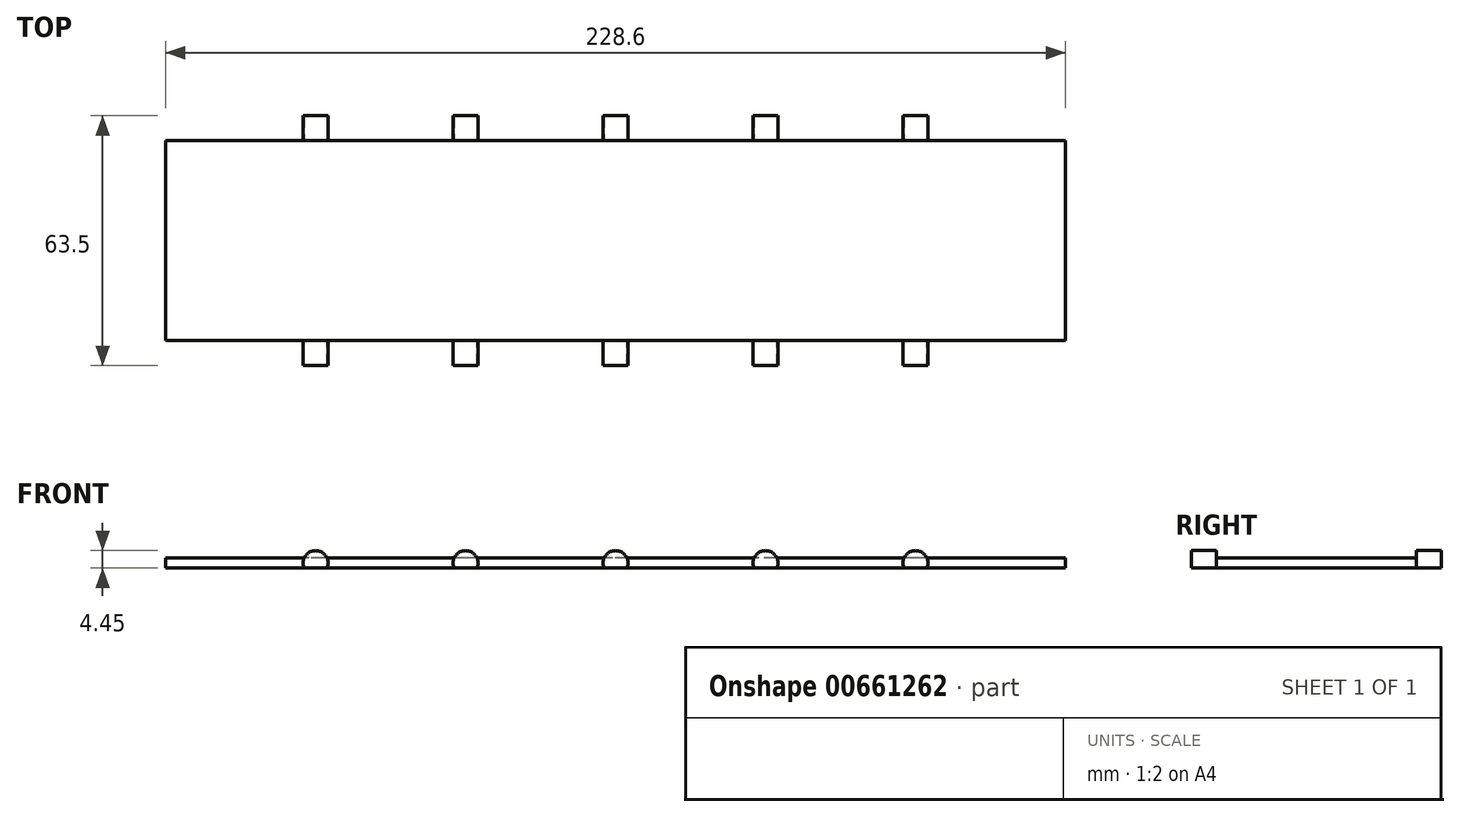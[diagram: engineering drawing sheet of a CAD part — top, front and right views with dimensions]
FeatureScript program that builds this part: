
annotation { "Feature Type Name" : "Feature", "Feature Type Description" : "" }
export const myFeature = defineFeature(function(context is Context, id is Id, definition is map)
    precondition{}
    {
        {
            var Q0;
            Q0=qCreatedBy(makeId("Top.planeOp"),FACE);
            var sketch = newSketch(context, id + "F0", { "sketchPlane" : qUnion([Q0])});
            skLineSegment(sketch, "E0.bottom", {"start": v(114.3, 25.4) * mm, "end": v(-114.3, 25.4) * mm});
            skLineSegment(sketch, "E0.top", {"start": v(114.3, -25.4) * mm, "end": v(-114.3, -25.4) * mm});
            skLineSegment(sketch, "E0.left", {"start": v(114.3, 25.4) * mm, "end": v(114.3, -25.4) * mm});
            skLineSegment(sketch, "E0.right", {"start": v(-114.3, 25.4) * mm, "end": v(-114.3, -25.4) * mm});
            skPoint(sketch, "E0.middle", {"position": v(0, 0) * mm});
            skLineSegment(sketch, "E1", {"start": v(0, 0) * mm, "end": v(-114.3, 0) * mm, "construction": true});
            skLineSegment(sketch, "E2", {"start": v(0, 0) * mm, "end": v(114.3, 0) * mm, "construction": true});
            skLineSegment(sketch, "E3", {"start": v(-38.1, 25.4) * mm, "end": v(-38.1, -25.4) * mm, "construction": true});
            skLineSegment(sketch, "E4", {"start": v(-76.2, 25.4) * mm, "end": v(-76.2, -25.4) * mm, "construction": true});
            skLineSegment(sketch, "E5", {"start": v(0, 25.4) * mm, "end": v(0, -25.4) * mm, "construction": true});
            skLineSegment(sketch, "E6", {"start": v(38.1, 25.4) * mm, "end": v(38.1, -25.4) * mm, "construction": true});
            skLineSegment(sketch, "E7", {"start": v(76.2, -25.4) * mm, "end": v(76.2, 25.4) * mm, "construction": true});
            skSolve(sketch);
        }
        {
            var Q0;
            Q0=makeQuery(id+"F0.imprint","IMPRINT",FACE,{"disambiguationData":[TD([[makeQuery(id+"F0.imprint","IMPRINT",EDGE,{"derivedFrom":sQuery(id+"F0.wireOp",EDGE,"E0.bottom")}),1.0]])]});
            extrude(context, id + "F1", {"entities" : qUnion([Q0]), "depth" : 2.54 * mm, "offsetDistance" : 25.4 * mm});
        }
        {
            var Q0;
            Q0=makeQuery(id+"F1.opExtrude","SWEPT_FACE",FACE,{"disambiguationData":[OSD([sQuery(id+"F0.wireOp",EDGE,"E0.top")])]});
            var sketch = newSketch(context, id + "F2", { "sketchPlane" : qUnion([Q0])});
            skLineSegment(sketch, "E8.0.0", {"start": v(-114.3, 0) * mm, "end": v(-79.1, 0) * mm, "construction": true});
            skLineSegment(sketch, "E8.0.1", {"start": v(114.3, 0) * mm, "end": v(114.3, 2.54) * mm, "construction": true});
            skLineSegment(sketch, "E8.0.3", {"start": v(-114.3, 2.54) * mm, "end": v(-114.3, 0) * mm, "construction": true});
            skLineSegment(sketch, "E9", {"start": v(0, 0) * mm, "end": v(0, 2.54) * mm, "construction": true});
            skLineSegment(sketch, "E10", {"start": v(-3.17, 1.27) * mm, "end": v(-34.93, 1.27) * mm, "construction": true});
            skLineSegment(sketch, "E11", {"start": v(3.18, 1.27) * mm, "end": v(34.93, 1.27) * mm, "construction": true});
            skLineSegment(sketch, "E12", {"start": v(-76.2, 2.54) * mm, "end": v(-76.2, 0) * mm, "construction": true});
            skLineSegment(sketch, "E13", {"start": v(-38.1, 2.54) * mm, "end": v(-38.1, 0) * mm, "construction": true});
            skLineSegment(sketch, "E14", {"start": v(0, 2.54) * mm, "end": v(0, 0) * mm, "construction": true});
            skLineSegment(sketch, "E15", {"start": v(38.1, 2.54) * mm, "end": v(38.1, 0) * mm, "construction": true});
            skLineSegment(sketch, "E16", {"start": v(76.2, 2.54) * mm, "end": v(76.2, 0) * mm, "construction": true});
            skCircle(sketch, "E17", {"center": v(-76.2, 1.27) * mm, "radius": 3.18 * mm});
            skCircle(sketch, "E18", {"center": v(-38.1, 1.27) * mm, "radius": 3.18 * mm});
            skCircle(sketch, "E19", {"center": v(0, 1.27) * mm, "radius": 3.18 * mm});
            skCircle(sketch, "E20", {"center": v(38.1, 1.27) * mm, "radius": 3.18 * mm});
            skCircle(sketch, "E21", {"center": v(76.2, 1.27) * mm, "radius": 3.18 * mm});
            skLineSegment(sketch, "E22.trimOffspring", {"start": v(-73.3, 0) * mm, "end": v(-41, 0) * mm, "construction": true});
            skLineSegment(sketch, "E23.trimOffspring", {"start": v(-79.1, 2.54) * mm, "end": v(-114.3, 2.54) * mm, "construction": true});
            skLineSegment(sketch, "E24.trimOffspring", {"start": v(-79.38, 1.27) * mm, "end": v(-114.3, 1.27) * mm, "construction": true});
            skLineSegment(sketch, "E25.trimOffspring", {"start": v(-41, 2.54) * mm, "end": v(-73.3, 2.54) * mm, "construction": true});
            skLineSegment(sketch, "E26.trimOffspring", {"start": v(-41.27, 1.27) * mm, "end": v(-73.03, 1.27) * mm, "construction": true});
            skLineSegment(sketch, "E27.trimOffspring", {"start": v(-35.2, 0) * mm, "end": v(-2.9, 0) * mm, "construction": true});
            skLineSegment(sketch, "E28.trimOffspring", {"start": v(2.9, 0) * mm, "end": v(35.2, 0) * mm, "construction": true});
            skLineSegment(sketch, "E29.trimOffspring", {"start": v(41.27, 1.27) * mm, "end": v(73.03, 1.27) * mm, "construction": true});
            skLineSegment(sketch, "E30.trimOffspring", {"start": v(79.38, 1.27) * mm, "end": v(114.3, 1.27) * mm, "construction": true});
            skLineSegment(sketch, "E31.trimOffspring", {"start": v(73.3, 2.54) * mm, "end": v(41, 2.54) * mm, "construction": true});
            skLineSegment(sketch, "E32.trimOffspring", {"start": v(79.1, 0) * mm, "end": v(114.3, 0) * mm, "construction": true});
            skSolve(sketch);
        }
        {
            var Q0;
            {var subQ0=sQuery(id+"F2.wireOp",EDGE,"E17");var subQ1=makeQuery(id+"F1.opExtrude","CAP_EDGE",EDGE,{"disambiguationData":[OSD([sQuery(id+"F0.wireOp",EDGE,"E0.top")])],"isStart":true});var subQ2=makeQuery(id+"F2.imprint","INTERSECT",VERTEX,{"disambiguationData":[OD(0.0)],"derivedFrom":[subQ1,subQ0]});Q0=makeQuery(id+"F2.imprint","IMPRINT",FACE,{"disambiguationData":[TD([[makeQuery(id+"F2.imprint","IMPRINT",EDGE,{"disambiguationData":[TD([[subQ2,-1.0]])],"derivedFrom":subQ0}),1.0]])]});}
            var Q1;
            {var subQ0=sQuery(id+"F2.wireOp",EDGE,"E17");var subQ1=sQuery(id+"F0.wireOp",EDGE,"E0.top");var subQ2=makeQuery(id+"F1.opExtrude","CAP_EDGE",EDGE,{"disambiguationData":[OSD([subQ1])],"isStart":false});var subQ3=makeQuery(id+"F2.imprint","INTERSECT",VERTEX,{"disambiguationData":[OD(0.0)],"derivedFrom":[subQ2,subQ0]});Q1=makeQuery(id+"F2.imprint","IMPRINT",FACE,{"disambiguationData":[TD([[makeQuery(id+"F2.imprint","IMPRINT",EDGE,{"disambiguationData":[TD([[subQ3,-1.0]])],"derivedFrom":subQ0}),1.0]])]});}
            var Q2;
            {var subQ0=sQuery(id+"F2.wireOp",EDGE,"E17");var subQ1=makeQuery(id+"F1.opExtrude","CAP_EDGE",EDGE,{"disambiguationData":[OSD([sQuery(id+"F0.wireOp",EDGE,"E0.top")])],"isStart":false});var subQ2=makeQuery(id+"F2.imprint","INTERSECT",VERTEX,{"disambiguationData":[OD(0.0)],"derivedFrom":[subQ1,subQ0]});Q2=makeQuery(id+"F2.imprint","IMPRINT",FACE,{"disambiguationData":[TD([[makeQuery(id+"F2.imprint","IMPRINT",EDGE,{"disambiguationData":[TD([[subQ2,1.0]])],"derivedFrom":subQ0}),1.0]])]});}
            var Q3;
            {var subQ0=sQuery(id+"F2.wireOp",EDGE,"E18");var subQ1=makeQuery(id+"F1.opExtrude","CAP_EDGE",EDGE,{"disambiguationData":[OSD([sQuery(id+"F0.wireOp",EDGE,"E0.top")])],"isStart":true});var subQ2=makeQuery(id+"F2.imprint","INTERSECT",VERTEX,{"disambiguationData":[OD(0.0)],"derivedFrom":[subQ1,subQ0]});Q3=makeQuery(id+"F2.imprint","IMPRINT",FACE,{"disambiguationData":[TD([[makeQuery(id+"F2.imprint","IMPRINT",EDGE,{"disambiguationData":[TD([[subQ2,-1.0]])],"derivedFrom":subQ0}),1.0]])]});}
            var Q4;
            {var subQ0=sQuery(id+"F2.wireOp",EDGE,"E18");var subQ1=sQuery(id+"F0.wireOp",EDGE,"E0.top");var subQ2=makeQuery(id+"F1.opExtrude","CAP_EDGE",EDGE,{"disambiguationData":[OSD([subQ1])],"isStart":false});var subQ3=makeQuery(id+"F2.imprint","INTERSECT",VERTEX,{"disambiguationData":[OD(0.0)],"derivedFrom":[subQ2,subQ0]});Q4=makeQuery(id+"F2.imprint","IMPRINT",FACE,{"disambiguationData":[TD([[makeQuery(id+"F2.imprint","IMPRINT",EDGE,{"disambiguationData":[TD([[subQ3,-1.0]])],"derivedFrom":subQ0}),1.0]])]});}
            var Q5;
            {var subQ0=sQuery(id+"F2.wireOp",EDGE,"E18");var subQ1=makeQuery(id+"F1.opExtrude","CAP_EDGE",EDGE,{"disambiguationData":[OSD([sQuery(id+"F0.wireOp",EDGE,"E0.top")])],"isStart":false});var subQ2=makeQuery(id+"F2.imprint","INTERSECT",VERTEX,{"disambiguationData":[OD(0.0)],"derivedFrom":[subQ1,subQ0]});Q5=makeQuery(id+"F2.imprint","IMPRINT",FACE,{"disambiguationData":[TD([[makeQuery(id+"F2.imprint","IMPRINT",EDGE,{"disambiguationData":[TD([[subQ2,1.0]])],"derivedFrom":subQ0}),1.0]])]});}
            var Q6;
            {var subQ0=sQuery(id+"F2.wireOp",EDGE,"E19");var subQ1=makeQuery(id+"F1.opExtrude","CAP_EDGE",EDGE,{"disambiguationData":[OSD([sQuery(id+"F0.wireOp",EDGE,"E0.top")])],"isStart":true});var subQ2=makeQuery(id+"F2.imprint","INTERSECT",VERTEX,{"disambiguationData":[OD(0.0)],"derivedFrom":[subQ1,subQ0]});Q6=makeQuery(id+"F2.imprint","IMPRINT",FACE,{"disambiguationData":[TD([[makeQuery(id+"F2.imprint","IMPRINT",EDGE,{"disambiguationData":[TD([[subQ2,-1.0]])],"derivedFrom":subQ0}),1.0]])]});}
            var Q7;
            {var subQ0=sQuery(id+"F2.wireOp",EDGE,"E19");var subQ1=sQuery(id+"F0.wireOp",EDGE,"E0.top");var subQ2=makeQuery(id+"F1.opExtrude","CAP_EDGE",EDGE,{"disambiguationData":[OSD([subQ1])],"isStart":false});var subQ3=makeQuery(id+"F2.imprint","INTERSECT",VERTEX,{"disambiguationData":[OD(0.0)],"derivedFrom":[subQ2,subQ0]});Q7=makeQuery(id+"F2.imprint","IMPRINT",FACE,{"disambiguationData":[TD([[makeQuery(id+"F2.imprint","IMPRINT",EDGE,{"disambiguationData":[TD([[subQ3,-1.0]])],"derivedFrom":subQ0}),1.0]])]});}
            var Q8;
            {var subQ0=sQuery(id+"F2.wireOp",EDGE,"E19");var subQ1=makeQuery(id+"F1.opExtrude","CAP_EDGE",EDGE,{"disambiguationData":[OSD([sQuery(id+"F0.wireOp",EDGE,"E0.top")])],"isStart":false});var subQ2=makeQuery(id+"F2.imprint","INTERSECT",VERTEX,{"disambiguationData":[OD(0.0)],"derivedFrom":[subQ1,subQ0]});Q8=makeQuery(id+"F2.imprint","IMPRINT",FACE,{"disambiguationData":[TD([[makeQuery(id+"F2.imprint","IMPRINT",EDGE,{"disambiguationData":[TD([[subQ2,1.0]])],"derivedFrom":subQ0}),1.0]])]});}
            var Q9;
            {var subQ0=sQuery(id+"F2.wireOp",EDGE,"E20");var subQ1=makeQuery(id+"F1.opExtrude","CAP_EDGE",EDGE,{"disambiguationData":[OSD([sQuery(id+"F0.wireOp",EDGE,"E0.top")])],"isStart":false});var subQ2=makeQuery(id+"F2.imprint","INTERSECT",VERTEX,{"disambiguationData":[OD(0.0)],"derivedFrom":[subQ1,subQ0]});Q9=makeQuery(id+"F2.imprint","IMPRINT",FACE,{"disambiguationData":[TD([[makeQuery(id+"F2.imprint","IMPRINT",EDGE,{"disambiguationData":[TD([[subQ2,1.0]])],"derivedFrom":subQ0}),1.0]])]});}
            var Q10;
            {var subQ0=sQuery(id+"F2.wireOp",EDGE,"E20");var subQ1=sQuery(id+"F0.wireOp",EDGE,"E0.top");var subQ2=makeQuery(id+"F1.opExtrude","CAP_EDGE",EDGE,{"disambiguationData":[OSD([subQ1])],"isStart":false});var subQ3=makeQuery(id+"F2.imprint","INTERSECT",VERTEX,{"disambiguationData":[OD(0.0)],"derivedFrom":[subQ2,subQ0]});Q10=makeQuery(id+"F2.imprint","IMPRINT",FACE,{"disambiguationData":[TD([[makeQuery(id+"F2.imprint","IMPRINT",EDGE,{"disambiguationData":[TD([[subQ3,-1.0]])],"derivedFrom":subQ0}),1.0]])]});}
            var Q11;
            {var subQ0=sQuery(id+"F2.wireOp",EDGE,"E20");var subQ1=makeQuery(id+"F1.opExtrude","CAP_EDGE",EDGE,{"disambiguationData":[OSD([sQuery(id+"F0.wireOp",EDGE,"E0.top")])],"isStart":true});var subQ2=makeQuery(id+"F2.imprint","INTERSECT",VERTEX,{"disambiguationData":[OD(0.0)],"derivedFrom":[subQ1,subQ0]});Q11=makeQuery(id+"F2.imprint","IMPRINT",FACE,{"disambiguationData":[TD([[makeQuery(id+"F2.imprint","IMPRINT",EDGE,{"disambiguationData":[TD([[subQ2,-1.0]])],"derivedFrom":subQ0}),1.0]])]});}
            var Q12;
            {var subQ0=sQuery(id+"F2.wireOp",EDGE,"E21");var subQ1=makeQuery(id+"F1.opExtrude","CAP_EDGE",EDGE,{"disambiguationData":[OSD([sQuery(id+"F0.wireOp",EDGE,"E0.top")])],"isStart":true});var subQ2=makeQuery(id+"F2.imprint","INTERSECT",VERTEX,{"disambiguationData":[OD(0.0)],"derivedFrom":[subQ1,subQ0]});Q12=makeQuery(id+"F2.imprint","IMPRINT",FACE,{"disambiguationData":[TD([[makeQuery(id+"F2.imprint","IMPRINT",EDGE,{"disambiguationData":[TD([[subQ2,-1.0]])],"derivedFrom":subQ0}),1.0]])]});}
            var Q13;
            {var subQ0=sQuery(id+"F2.wireOp",EDGE,"E21");var subQ1=sQuery(id+"F0.wireOp",EDGE,"E0.top");var subQ2=makeQuery(id+"F1.opExtrude","CAP_EDGE",EDGE,{"disambiguationData":[OSD([subQ1])],"isStart":false});var subQ3=makeQuery(id+"F2.imprint","INTERSECT",VERTEX,{"disambiguationData":[OD(0.0)],"derivedFrom":[subQ2,subQ0]});Q13=makeQuery(id+"F2.imprint","IMPRINT",FACE,{"disambiguationData":[TD([[makeQuery(id+"F2.imprint","IMPRINT",EDGE,{"disambiguationData":[TD([[subQ3,-1.0]])],"derivedFrom":subQ0}),1.0]])]});}
            var Q14;
            {var subQ0=sQuery(id+"F2.wireOp",EDGE,"E21");var subQ1=makeQuery(id+"F1.opExtrude","CAP_EDGE",EDGE,{"disambiguationData":[OSD([sQuery(id+"F0.wireOp",EDGE,"E0.top")])],"isStart":false});var subQ2=makeQuery(id+"F2.imprint","INTERSECT",VERTEX,{"disambiguationData":[OD(0.0)],"derivedFrom":[subQ1,subQ0]});Q14=makeQuery(id+"F2.imprint","IMPRINT",FACE,{"disambiguationData":[TD([[makeQuery(id+"F2.imprint","IMPRINT",EDGE,{"disambiguationData":[TD([[subQ2,1.0]])],"derivedFrom":subQ0}),1.0]])]});}
            extrude(context, id + "F3", {"entities" : qUnion([Q0, Q1, Q2, Q3, Q4, Q5, Q6, Q7, Q8, Q9, Q10, Q11, Q12, Q13, Q14]), "depth" : 6.35 * mm, "offsetDistance" : 25.4 * mm});
        }
        {
            var Q0;
            Q0=makeQuery(id+"F3.opExtrude","SWEPT_BODY",BODY,{"disambiguationData":[OSD([sQuery(id+"F2.wireOp",EDGE,"E17")])]});
            var Q1;
            Q1=makeQuery(id+"F3.opExtrude","SWEPT_BODY",BODY,{"disambiguationData":[OSD([sQuery(id+"F2.wireOp",EDGE,"E18")])]});
            var Q2;
            Q2=makeQuery(id+"F3.opExtrude","SWEPT_BODY",BODY,{"disambiguationData":[OSD([sQuery(id+"F2.wireOp",EDGE,"E19")])]});
            var Q3;
            Q3=makeQuery(id+"F3.opExtrude","SWEPT_BODY",BODY,{"disambiguationData":[OSD([sQuery(id+"F2.wireOp",EDGE,"E20")])]});
            var Q4;
            Q4=makeQuery(id+"F3.opExtrude","SWEPT_BODY",BODY,{"disambiguationData":[OSD([sQuery(id+"F2.wireOp",EDGE,"E21")])]});
            var Q5;
            Q5=qCreatedBy(makeId("Front.planeOp"),FACE);
            mirror(context, id + "F4", {"entities" : qUnion([Q0, Q1, Q2, Q3, Q4]), "mirrorPlane" : qUnion([Q5])});
        }
    });
